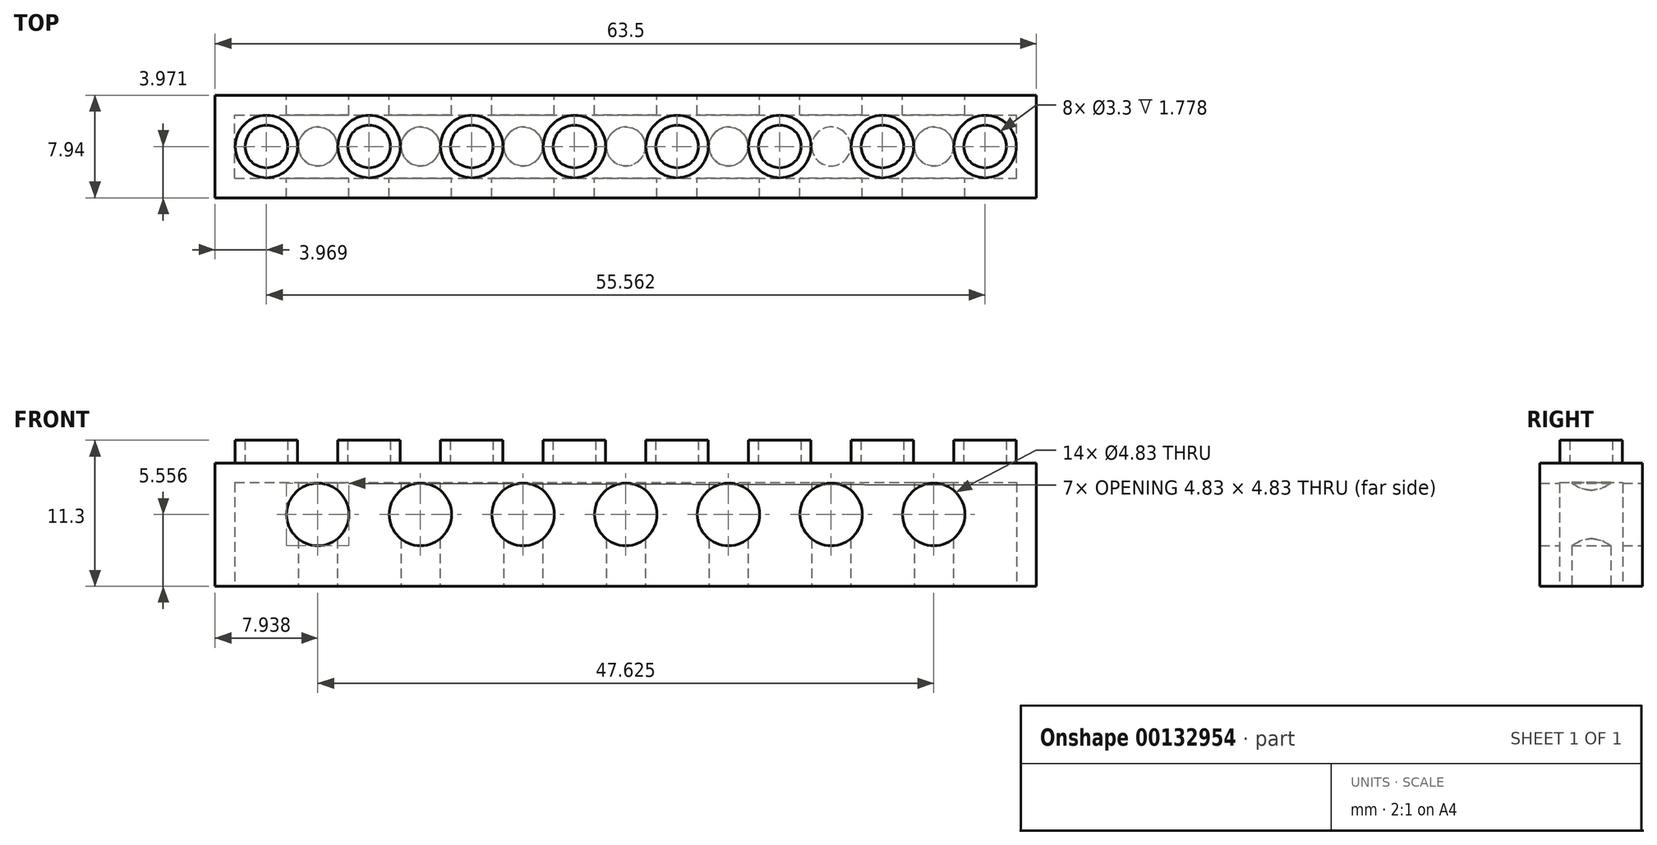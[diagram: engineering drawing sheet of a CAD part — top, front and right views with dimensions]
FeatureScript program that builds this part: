
annotation { "Feature Type Name" : "Feature", "Feature Type Description" : "" }
export const myFeature = defineFeature(function(context is Context, id is Id, definition is map)
    precondition{}
    {
        {
            var Q0;
            Q0=qCreatedBy(makeId("Front.planeOp"),FACE);
            var sketch = newSketch(context, id + "F0", { "sketchPlane" : qUnion([Q0])});
            skLineSegment(sketch, "E0.bottom", {"start": v(0, 9.53) * mm, "end": v(63.5, 9.53) * mm});
            skLineSegment(sketch, "E0.top", {"start": v(0, 0) * mm, "end": v(63.5, 0) * mm});
            skLineSegment(sketch, "E0.left", {"start": v(0, 9.53) * mm, "end": v(0, 0) * mm});
            skLineSegment(sketch, "E0.right", {"start": v(63.5, 9.53) * mm, "end": v(63.5, 0) * mm});
            skSolve(sketch);
        }
        {
            var Q0;
            Q0 = qSketchRegion(id + "F0", true);
            extrude(context, id + "F1", {"entities" : qUnion([Q0]), "depth" : 7.94 * mm});
        }
        {
            var Q0;
            Q0=makeQuery(id+"F1.opExtrude","SWEPT_FACE",FACE,{"disambiguationData":[OSD([sQuery(id+"F0.wireOp",EDGE,"E0.bottom")])]});
            var sketch = newSketch(context, id + "F2", { "sketchPlane" : qUnion([Q0])});
            skCircle(sketch, "E1", {"center": v(3.97, -3.97) * mm, "radius": 2.41 * mm});
            skCircle(sketch, "E2", {"center": v(11.9, -3.97) * mm, "radius": 2.41 * mm});
            skCircle(sketch, "E3", {"center": v(19.84, -3.97) * mm, "radius": 2.41 * mm});
            skCircle(sketch, "E4", {"center": v(35.72, -3.97) * mm, "radius": 2.41 * mm});
            skCircle(sketch, "E5", {"center": v(27.78, -3.97) * mm, "radius": 2.41 * mm});
            skCircle(sketch, "E6", {"center": v(43.66, -3.97) * mm, "radius": 2.41 * mm});
            skCircle(sketch, "E7", {"center": v(51.6, -3.97) * mm, "radius": 2.41 * mm});
            skCircle(sketch, "E8", {"center": v(59.53, -3.97) * mm, "radius": 2.41 * mm});
            skLineSegment(sketch, "E9", {"start": v(-3.97, -3.97) * mm, "end": v(3.97, -3.97) * mm, "construction": true});
            skLineSegment(sketch, "E10", {"start": v(3.97, -3.97) * mm, "end": v(11.9, -3.97) * mm, "construction": true});
            skLineSegment(sketch, "E11", {"start": v(11.9, -3.97) * mm, "end": v(19.84, -3.97) * mm, "construction": true});
            skLineSegment(sketch, "E12", {"start": v(19.84, -3.97) * mm, "end": v(27.78, -3.97) * mm, "construction": true});
            skLineSegment(sketch, "E13", {"start": v(27.78, -3.97) * mm, "end": v(35.72, -3.97) * mm, "construction": true});
            skLineSegment(sketch, "E14", {"start": v(35.72, -3.97) * mm, "end": v(43.66, -3.97) * mm, "construction": true});
            skLineSegment(sketch, "E15", {"start": v(43.66, -3.97) * mm, "end": v(51.6, -3.97) * mm, "construction": true});
            skLineSegment(sketch, "E16", {"start": v(51.6, -3.97) * mm, "end": v(59.53, -3.97) * mm, "construction": true});
            skLineSegment(sketch, "E17", {"start": v(59.53, -3.97) * mm, "end": v(67.47, -3.97) * mm, "construction": true});
            skCircle(sketch, "E18", {"center": v(3.97, -3.97) * mm, "radius": 1.65 * mm});
            skCircle(sketch, "E19", {"center": v(11.9, -3.97) * mm, "radius": 1.65 * mm});
            skCircle(sketch, "E20", {"center": v(19.84, -3.97) * mm, "radius": 1.65 * mm});
            skCircle(sketch, "E21", {"center": v(27.78, -3.97) * mm, "radius": 1.65 * mm});
            skCircle(sketch, "E22", {"center": v(35.72, -3.97) * mm, "radius": 1.65 * mm});
            skCircle(sketch, "E23", {"center": v(43.66, -3.97) * mm, "radius": 1.65 * mm});
            skCircle(sketch, "E24", {"center": v(51.6, -3.97) * mm, "radius": 1.65 * mm});
            skCircle(sketch, "E25", {"center": v(59.53, -3.97) * mm, "radius": 1.65 * mm});
            skPoint(sketch, "E26", {"position": v(63.5, -3.97) * mm});
            skPoint(sketch, "E27", {"position": v(0, -3.97) * mm});
            skSolve(sketch);
        }
        {
            var Q0;
            Q0 = qSketchRegion(id + "F2", true);
            extrude(context, id + "F3", {"entities" : qUnion([Q0]), "operationType" : NewBodyOperationType.ADD, "depth" : 1.78 * mm});
        }
        {
            var Q0;
            Q0=qCreatedBy(makeId("Front.planeOp"),FACE);
            var sketch = newSketch(context, id + "F4", { "sketchPlane" : qUnion([Q0])});
            skCircle(sketch, "E28", {"center": v(7.94, 5.56) * mm, "radius": 2.41 * mm});
            skCircle(sketch, "E29", {"center": v(15.88, 5.56) * mm, "radius": 2.41 * mm});
            skCircle(sketch, "E30", {"center": v(23.81, 5.56) * mm, "radius": 2.41 * mm});
            skCircle(sketch, "E31", {"center": v(31.75, 5.56) * mm, "radius": 2.41 * mm});
            skCircle(sketch, "E32", {"center": v(39.69, 5.56) * mm, "radius": 2.41 * mm});
            skCircle(sketch, "E33", {"center": v(47.62, 5.56) * mm, "radius": 2.41 * mm});
            skCircle(sketch, "E34", {"center": v(55.56, 5.56) * mm, "radius": 2.41 * mm});
            skLineSegment(sketch, "E35", {"start": v(0, 5.56) * mm, "end": v(7.94, 5.56) * mm, "construction": true});
            skLineSegment(sketch, "E36", {"start": v(7.94, 5.56) * mm, "end": v(15.88, 5.56) * mm, "construction": true});
            skLineSegment(sketch, "E37", {"start": v(15.88, 5.56) * mm, "end": v(23.81, 5.56) * mm, "construction": true});
            skLineSegment(sketch, "E38", {"start": v(23.81, 5.56) * mm, "end": v(31.75, 5.56) * mm, "construction": true});
            skLineSegment(sketch, "E39", {"start": v(31.75, 5.56) * mm, "end": v(39.69, 5.56) * mm, "construction": true});
            skLineSegment(sketch, "E40", {"start": v(39.69, 5.56) * mm, "end": v(47.62, 5.56) * mm, "construction": true});
            skLineSegment(sketch, "E41", {"start": v(47.62, 5.56) * mm, "end": v(55.56, 5.56) * mm, "construction": true});
            skLineSegment(sketch, "E42", {"start": v(55.56, 5.56) * mm, "end": v(63.5, 5.56) * mm, "construction": true});
            skSolve(sketch);
        }
        {
            var Q0;
            Q0=makeQuery(id+"F1.opExtrude","SWEPT_FACE",FACE,{"disambiguationData":[OSD([sQuery(id+"F0.wireOp",EDGE,"E0.top")])]});
            var sketch = newSketch(context, id + "F5", { "sketchPlane" : qUnion([Q0])});
            skLineSegment(sketch, "E43.bottom", {"start": v(1.52, 6.41) * mm, "end": v(61.98, 6.41) * mm});
            skLineSegment(sketch, "E43.top", {"start": v(1.52, 1.52) * mm, "end": v(61.98, 1.52) * mm});
            skLineSegment(sketch, "E43.left", {"start": v(1.52, 6.41) * mm, "end": v(1.52, 1.52) * mm});
            skLineSegment(sketch, "E43.right", {"start": v(61.98, 6.41) * mm, "end": v(61.98, 1.52) * mm});
            skLineSegment(sketch, "E44", {"start": v(0, 3.97) * mm, "end": v(7.94, 3.97) * mm, "construction": true});
            skLineSegment(sketch, "E45", {"start": v(7.94, 3.97) * mm, "end": v(15.88, 3.97) * mm, "construction": true});
            skLineSegment(sketch, "E46", {"start": v(15.88, 3.97) * mm, "end": v(23.81, 3.97) * mm, "construction": true});
            skLineSegment(sketch, "E47", {"start": v(23.81, 3.97) * mm, "end": v(31.75, 3.97) * mm, "construction": true});
            skLineSegment(sketch, "E48", {"start": v(31.75, 3.97) * mm, "end": v(39.69, 3.97) * mm, "construction": true});
            skLineSegment(sketch, "E49", {"start": v(39.69, 3.97) * mm, "end": v(47.62, 3.97) * mm, "construction": true});
            skLineSegment(sketch, "E50", {"start": v(47.62, 3.97) * mm, "end": v(55.56, 3.97) * mm, "construction": true});
            skLineSegment(sketch, "E51", {"start": v(55.56, 3.97) * mm, "end": v(63.5, 3.97) * mm, "construction": true});
            skCircle(sketch, "E52", {"center": v(7.94, 3.97) * mm, "radius": 1.51 * mm});
            skCircle(sketch, "E53", {"center": v(15.88, 3.97) * mm, "radius": 1.51 * mm});
            skCircle(sketch, "E54", {"center": v(23.81, 3.97) * mm, "radius": 1.51 * mm});
            skCircle(sketch, "E55", {"center": v(31.75, 3.97) * mm, "radius": 1.51 * mm});
            skCircle(sketch, "E56", {"center": v(39.69, 3.97) * mm, "radius": 1.51 * mm});
            skCircle(sketch, "E57", {"center": v(47.62, 3.97) * mm, "radius": 1.51 * mm});
            skCircle(sketch, "E58", {"center": v(55.56, 3.97) * mm, "radius": 1.51 * mm});
            skSolve(sketch);
        }
        {
            var Q0;
            Q0 = qSketchRegion(id + "F5", true);
            extrude(context, id + "F6", {"entities" : qUnion([Q0]), "operationType" : NewBodyOperationType.REMOVE, "oppositeDirection" : true, "depth" : 8.03 * mm});
        }
        {
            var Q0;
            Q0 = qSketchRegion(id + "F4", true);
            extrude(context, id + "F7", {"entities" : qUnion([Q0]), "operationType" : NewBodyOperationType.REMOVE, "endBound" : BoundingType.THROUGH_ALL, "depth" : 25.4 * mm});
        }
    });
